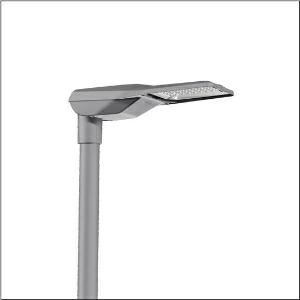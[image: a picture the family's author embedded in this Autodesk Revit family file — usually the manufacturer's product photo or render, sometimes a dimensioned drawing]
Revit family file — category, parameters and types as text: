
# Revit family: streetlight_sl_21_iq_mini___st0_5a_5xe2b41d08jb_1bd7
name_source: partatom
category: Lighting Fixtures
units: mm (PartAtom-declared; Revit-internal decimal feet)

## family parameters
Cut with Voids When Loaded = No
Host = Face
Light Source = No
Part Type = Normal
Room Calculation Point = No
Round Connector Dimension = Use Diameter
Shared = No

## types (1)
- --- (1 x LED, 11290 lm, 71.6 W, 4000K)
    Apparent Load = 72 VA
    CIE Flux Codes = 43 76 97 100 100
    Color Rendering = 70
    Color Temperature = 4000K
    Default Elevation = 1800 mm
    Description = Streetlight SL 21 iQ mini, mast luminaire, primary light control with lens, of PMMA, primary optical cover: cover, of toughened safety glass, transparent, light distribution: ST0.5a, light emission: direct distribution, primary light characteristic: asymmetric, installation type: post-top, side-entry, LED, High Power LED, rated luminous flux: 11.290lm, luminous efficacy: 158lm/W, light colour: 740, colour temperature: 4000K, control: Auto-Match, Temp-Guard, Lumen-Switch, Night-Set, Smart-Wire, Light-Fading, Desk-Remote (wireless, voltage-free reading and setting of iQ features in the workshop via application-optimized NFC function/RFID function), optimised constant luminous flux control (CLO 2.0), presetting dimming linear, mains connection: 220..240V, AC, 50/60Hz, start of lifetime: 72W, end of service life: 75W, reduction: 33W, luminaire housing, of diecast aluminium, powder-coated, Siteco® metallic grey (DB 702S), corrosivity category C5 mid according to DIN EN ISO 12944, please order mast flange separately, inclination adjustable: 0°, 5°, 10°, 15°, sealing non-destructively replaceable, multi-level sealing system, length: 628mm, width: 235mm, height: 110mm, mast flange for spigot size: 42mm (side-entry): 5XC10008XM4, 60/48mm (side-entry/post-top): 5XC10108XM2, 76/60mm (side-entry/post-top): 5XC10108XM1, protection rating (complete): IP66, insulation class (complete): insulation class II (safety insulation), certification: CE, ENEC, ENEC+, VDE, impact resistance: IK09, permissible operating ambient temperature for outdoor applications: -40..+50°C, standard-compliant lighting for roads and squares, packaging unit: 1 piece

Light Distribution: ST0.5a
    Height = 110 mm
    Lamp = 1 x LED
    Lamp Light Flux = 11290 lm
    Lamp Power = 71.6 W
    Lamp count = 1
    Length = 625 mm
    Luminous efficacy = 158 lm/W
    Manufacturer = Siteco
    ModVariant = No
    Model = 5XE2B41D08JB
    Number of Poles = 1
    OnlyDefault = Yes
    Power Factor = 1
    Product Name = Streetlight SL 21 iQ mini | ST0.5a
    Product group = mast luminaire | pylon top
    ProductGroupID = 6100
    Protection Class = Protection class II
    Protection Degree = IP 66
    RLX_Detail_Level = 1
    RLX_Emergency_Light_Flux = 0 lm
    RLX_Emergency_Type = 0
    RLX_Emergency_Type_DB = No
    RlxData = <blob elided: 103473 chars, md5=adaa7ef1>
    Socket = socket
    Standby Power = 0 W
    System Light Flux = 11290 lm
    System Power = 72 W
    Type Comments = factory setting: luminous flux: 100 % | dim-lin: 254 | 746 mA
    Type Image = l_1003519.jpg
    URL = http://relux.com
    VarID = @adj_104815
    Voltage = 0 V
    Weight = 0.00 kg
    Width = 234 mm

## geometry (parser evidence)
native form markers: Blend x4, Sweep x11
no freeform markers — native parametric forms only
